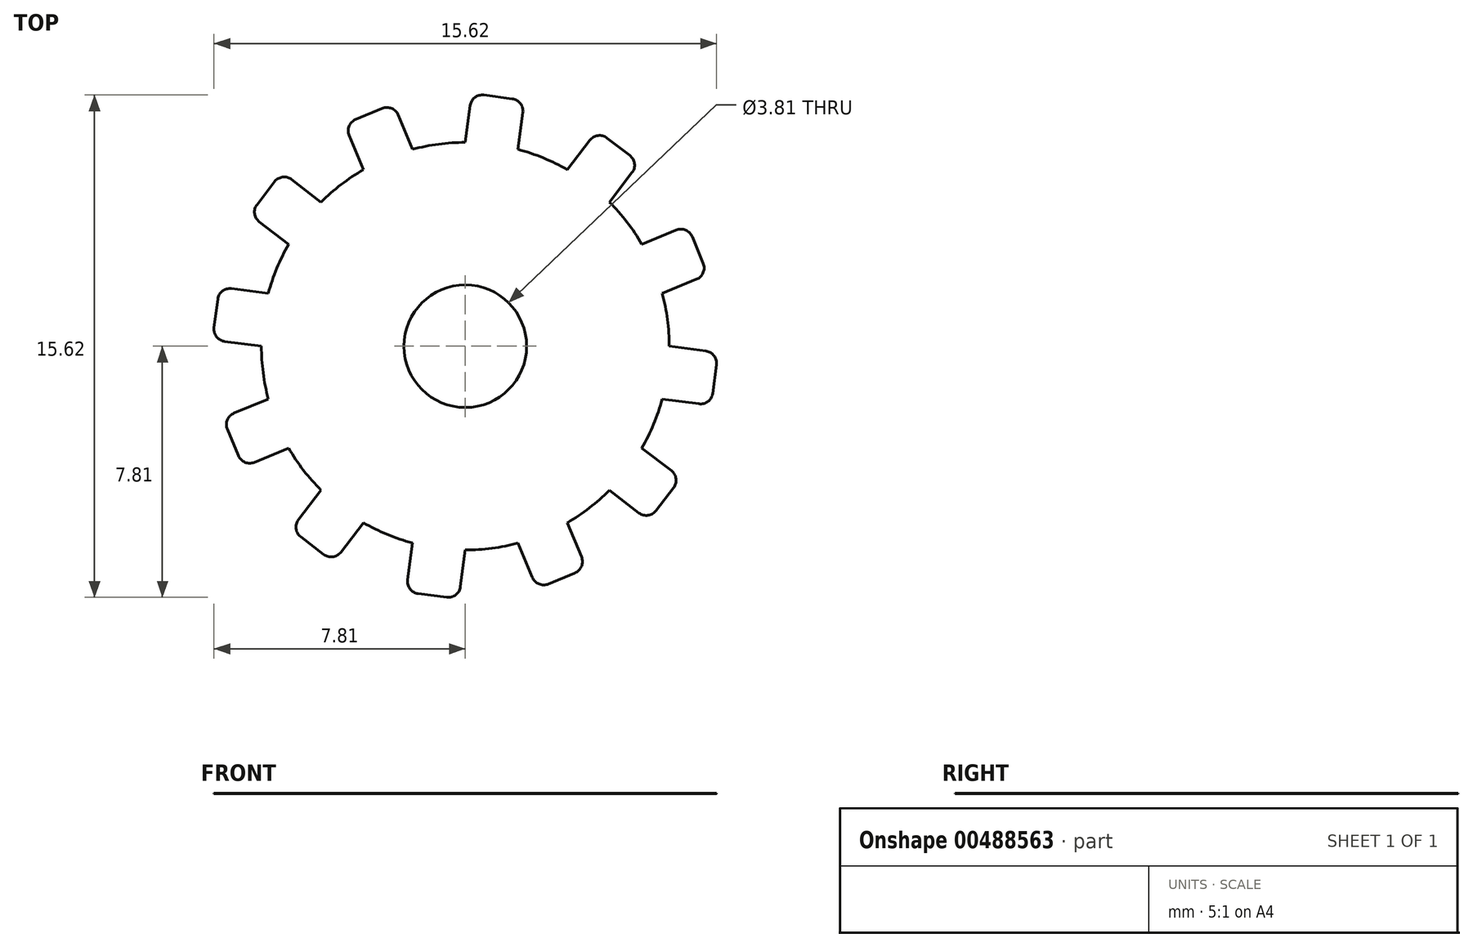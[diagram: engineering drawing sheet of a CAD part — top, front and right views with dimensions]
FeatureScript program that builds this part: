
annotation { "Feature Type Name" : "Feature", "Feature Type Description" : "" }
export const myFeature = defineFeature(function(context is Context, id is Id, definition is map)
    precondition{}
    {
        {
            var Q0;
            Q0=qCreatedBy(makeId("Top.planeOp"),FACE);
            var sketch = newSketch(context, id + "F0", { "sketchPlane" : qUnion([Q0])});
            skCircle(sketch, "E0", {"center": v(0, 0) * mm, "radius": 1.9 * mm});
            skCircle(sketch, "E1", {"center": v(0, 0) * mm, "radius": 6.34 * mm});
            skCircle(sketch, "E2", {"center": v(0, 0) * mm, "radius": 7.86 * mm, "construction": true});
            skLineSegment(sketch, "E3", {"start": v(0, 0) * mm, "end": v(5.57, 9.65) * mm, "construction": true});
            skLineSegment(sketch, "E4", {"start": v(0, 0) * mm, "end": v(2.91, 10.86) * mm, "construction": true});
            skLineSegment(sketch, "E5", {"start": v(0, 0) * mm, "end": v(1.03, 7.8) * mm, "construction": true});
            skLineSegment(sketch, "E6", {"start": v(0, 6.34) * mm, "end": v(0.15, 7.48) * mm});
            skLineSegment(sketch, "E7", {"start": v(1.64, 6.12) * mm, "end": v(1.8, 7.27) * mm});
            skLineSegment(sketch, "E8", {"start": v(1.46, 7.7) * mm, "end": v(0.58, 7.8) * mm});
            skPoint(sketch, "E9.visualSharp", {"position": v(0.2, 7.86) * mm});
            skArc(sketch, "E9.filletArc", {"start": v(0.58, 7.8) * mm, "mid": v(0.3, 7.73) * mm, "end": v(0.15, 7.48) * mm});
            skPoint(sketch, "E10.visualSharp", {"position": v(1.84, 7.64) * mm});
            skArc(sketch, "E10.filletArc", {"start": v(1.8, 7.27) * mm, "mid": v(1.72, 7.55) * mm, "end": v(1.46, 7.7) * mm});
            skSolve(sketch);
        }
        {
            var Q0;
            Q0=makeQuery(id+"F0.imprint","IMPRINT",FACE,{"disambiguationData":[TD([[makeQuery(id+"F0.imprint","IMPRINT",EDGE,{"derivedFrom":sQuery(id+"F0.wireOp",EDGE,"E0")}),-1.0]])]});
            var Q1;
            {var subQ1=sQuery(id+"F0.wireOp",EDGE,"E6");Q1=makeQuery(id+"F0.imprint","IMPRINT",FACE,{"disambiguationData":[TD([[makeQuery(id+"F0.imprint","IMPRINT",EDGE,{"derivedFrom":subQ1}),-1.0]])]});}
            extrude(context, id + "F1", {"entities" : qUnion([Q0, Q1]), "depth" : 1 / 203.2 * mm});
        }
        {
            var Q0;
            Q0=makeQuery(id+"F1.opExtrude","SWEPT_BODY",BODY,{"disambiguationData":[OSD([sQuery(id+"F0.wireOp",EDGE,"E0"),sQuery(id+"F0.wireOp",EDGE,"E1"),sQuery(id+"F0.wireOp",EDGE,"E6"),sQuery(id+"F0.wireOp",EDGE,"E7"),sQuery(id+"F0.wireOp",EDGE,"E8"),sQuery(id+"F0.wireOp",EDGE,"E9.filletArc"),sQuery(id+"F0.wireOp",EDGE,"E10.filletArc")])]});
            var Q1;
            Q1=makeQuery(id+"F1.opExtrude","SWEPT_FACE",FACE,{"disambiguationData":[OSD([sQuery(id+"F0.wireOp",EDGE,"E1")])]});
            circularPattern(context, id + "F2", {"operationType" : NewBodyOperationType.ADD, "entities" : qUnion([Q0]), "axis" : qUnion([Q1]), "angle" : 360 * degree, "instanceCount" : 12, "equalSpace" : true});
        }
    });
